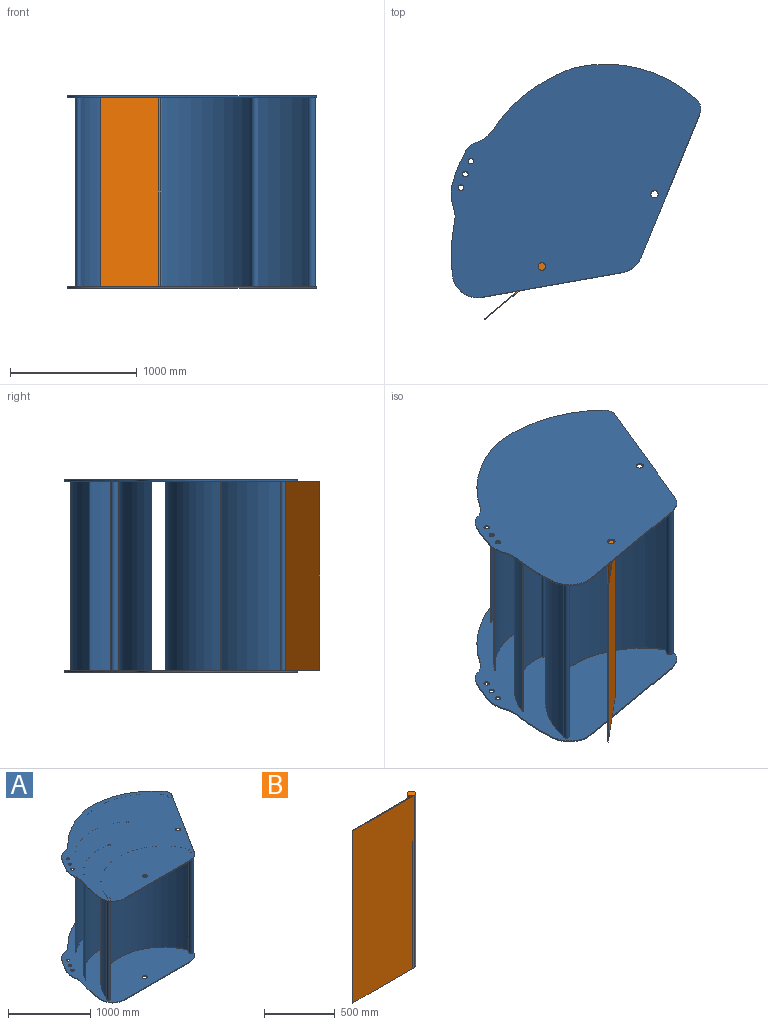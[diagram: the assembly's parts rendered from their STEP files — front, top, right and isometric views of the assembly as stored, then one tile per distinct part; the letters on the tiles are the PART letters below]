
ASSEMBLY  parts=2 mates=2
PART A: 61 faces, bbox 2164.2x1661x1520 mm
  f0: cylinder r=30.5mm len=61mm, axis (0,0,-1), area 1916.4mm2, adj f48,f49
  f1: cylinder r=29.5mm len=59mm, axis (0,0,-1), area 1853.5mm2, adj f48,f49
  f2: cylinder r=22mm len=44mm, axis (0,0,-1), area 1382.3mm2, adj f48,f49
  f3: cylinder r=22mm len=44mm, axis (0,0,-1), area 1382.3mm2, adj f48,f49
  f4: cylinder r=22mm len=44mm, axis (0,0,-1), area 1382.3mm2, adj f48,f49
  f5: cylinder r=326.18mm len=176.61mm, axis (0,0,-1), area 1797.7mm2, adj f48,f49,f50,f60
  f6: cylinder r=200mm len=212.82mm, axis (0,0,-1), area 3269.9mm2, adj f48,f49,f51,f52
  f7: cylinder r=20.5mm len=1500mm, axis (0,0,-1), area 183146.8mm2, adj f30,f44,f45,f49
  f8: cylinder r=30.5mm len=1500mm, axis (0,0,-1), area 272705.4mm2, adj f30,f44,f45,f46,f47,f49
  f9: cylinder r=15.5mm len=1500mm, axis (0,0,-1), area 135747.8mm2, adj f30,f41,f43,f49
  f10: cylinder r=15.5mm len=1500mm, axis (0,0,-1), area 136340.4mm2, adj f30,f37,f40,f49
  f11: cylinder r=30.5mm len=1500mm, axis (0,0,-1), area 274743.1mm2, adj f30,f32,f34,f35,f36,f49
  f12: cylinder r=30.5mm len=61mm, axis (0,0,-1), area 1916.4mm2, adj f30,f31
  f13: cylinder r=22mm len=44mm, axis (0,0,-1), area 1382.3mm2, adj f30,f31
  f14: cylinder r=22mm len=44mm, axis (0,0,-1), area 1382.3mm2, adj f30,f31
  f15: cylinder r=22mm len=44mm, axis (0,0,-1), area 1382.3mm2, adj f30,f31
  f16: cylinder r=29.5mm len=59mm, axis (0,0,-1), area 1853.5mm2, adj f30,f31
  f17: cylinder r=326.18mm len=176.61mm, axis (0,0,-1), area 1797.7mm2, adj f28,f29,f30,f31
  f18: cylinder r=200mm len=212.82mm, axis (0,0,-1), area 3269.9mm2, adj f19,f20,f30,f31
  f19: cylinder r=1403.06mm len=415.74mm, axis (0,0,-1), area 4273.2mm2, adj f18,f29,f30,f31
  f20: plane 1123.76x10mm, normal (0,-1,0), area 11237.6mm2, adj f18,f21,f30,f31
  f21: cylinder r=200mm len=169mm, axis (0,0,-1), area 2013.2mm2, adj f20,f22,f30,f31
  f22: plane 1036.5x655.9mm, normal (0.85,-0.53,0), area 12265.9mm2, adj f21,f23,f30,f31,f36,f47
  f23: cylinder r=100mm len=114.68mm, axis (0,0,-1), area 1222.9mm2, adj f22,f24,f30,f31
  f24: cylinder r=1074.34mm len=926.41mm, axis (0,0,-1), area 10568mm2, adj f23,f25,f30,f31
  f25: cylinder r=1282.61mm len=713.26mm, axis (0,0,-1), area 8227.7mm2, adj f24,f26,f30,f31
  f26: cylinder r=200mm len=117.51mm, axis (0,0,-1), area 1346.6mm2, adj f25,f27,f30,f31
  f27: cylinder r=186.95mm len=116.81mm, axis (0,0,-1), area 1363.1mm2, adj f26,f28,f30,f31
  f28: cylinder r=1324.47mm len=239.75mm, axis (0,0,-1), area 2828.3mm2, adj f17,f27,f30,f31
  f29: cylinder r=200mm len=107.43mm, axis (0,0,-1), area 1093.1mm2, adj f17,f19,f30,f31
  f30: plane 2164.16x1660.98mm, normal (0,0,1), area 2565292.9mm2, adj f7,f8,f9,f10,f11,f12,f13,f14
  f31: plane 2164.16x1660.98mm, normal (0,0,-1), area 2603609.2mm2, adj f12,f13,f14,f15,f16,f17,f18,f19
  f32: cylinder r=883.17mm len=1500mm, axis (0,0,-1), area 1936048.7mm2, adj f11,f30,f33,f49
  f33: plane 1500x5.5mm, normal (-0.92,-0.4,0), area 9000mm2, adj f30,f32,f34,f49
  f34: cylinder r=877.17mm len=1500mm, axis (0,0,-1), area 1914005.6mm2, adj f11,f30,f33,f49
  f35: plane 9.3x5.88mm, normal (0,0,1), area 3.7mm2, adj f11,f54
  f36: plane 9.3x5.88mm, normal (0,0,-1), area 3.7mm2, adj f11,f22
  f37: cylinder r=685.89mm len=1500mm, axis (0,0,-1), area 1444091.5mm2, adj f10,f30,f38,f49
  f38: plane 1500x4.62mm, normal (-0.77,-0.64,0), area 9000mm2, adj f30,f37,f39,f49
  f39: plane 1500x0.08mm, normal (0.65,-0.76,0), area 152.6mm2, adj f30,f38,f40,f49
  f40: cylinder r=679.89mm len=1500mm, axis (0,0,-1), area 1427930.9mm2, adj f10,f30,f39,f49
  f41: cylinder r=640.37mm len=1500mm, axis (0,0,-1), area 1242581.2mm2, adj f9,f30,f42,f49
  f42: plane 1500x5.24mm, normal (-0.49,-0.87,0), area 9000mm2, adj f30,f41,f43,f49
  f43: cylinder r=634.37mm len=1500mm, axis (0,0,-1), area 1226053.6mm2, adj f9,f30,f42,f49
  f44: cylinder r=755.25mm len=1500mm, axis (0,0,-1), area 2799788.5mm2, adj f7,f8,f30,f49
  f45: cylinder r=761.25mm len=1500mm, axis (0,0,-1), area 2838096.4mm2, adj f7,f8,f30,f49
  f46: plane 9.3x5.88mm, normal (0,0,1), area 3.7mm2, adj f8,f54
  f47: plane 9.3x5.88mm, normal (0,0,-1), area 3.7mm2, adj f8,f22
  f48: plane 2164.16x1660.98mm, normal (0,0,1), area 2603609.2mm2, adj f0,f1,f2,f3,f4,f5,f6,f50
  f49: plane 2164.16x1660.98mm, normal (0,0,-1), area 2565292.9mm2, adj f0,f1,f2,f3,f4,f5,f6,f7
  f50: cylinder r=200mm len=107.43mm, axis (0,0,-1), area 1093.1mm2, adj f5,f48,f49,f51
  f51: cylinder r=1403.06mm len=415.74mm, axis (0,0,-1), area 4273.2mm2, adj f6,f48,f49,f50
  f52: plane 1123.76x10mm, normal (0,-1,0), area 11237.6mm2, adj f6,f48,f49,f53
  f53: cylinder r=200mm len=169mm, axis (0,0,-1), area 2013.2mm2, adj f48,f49,f52,f54
  f54: plane 1036.5x655.9mm, normal (0.85,-0.53,0), area 12265.9mm2, adj f35,f46,f48,f49,f53,f55
  f55: cylinder r=100mm len=114.68mm, axis (0,0,-1), area 1222.9mm2, adj f48,f49,f54,f56
  f56: cylinder r=1074.34mm len=926.41mm, axis (0,0,-1), area 10568mm2, adj f48,f49,f55,f57
  f57: cylinder r=1282.61mm len=713.26mm, axis (0,0,-1), area 8227.7mm2, adj f48,f49,f56,f58
  f58: cylinder r=200mm len=117.51mm, axis (0,0,-1), area 1346.6mm2, adj f48,f49,f57,f59
  f59: cylinder r=186.95mm len=116.81mm, axis (0,0,-1), area 1363.1mm2, adj f48,f49,f58,f60
  f60: cylinder r=1324.47mm len=239.75mm, axis (0,0,-1), area 2828.3mm2, adj f5,f48,f49,f59
PART B: 6 faces, bbox 646.3x61x1490 mm
  f0: cylinder r=30.5mm len=1490mm, axis (0,0,-1), area 256544.7mm2, adj f1,f2,f4,f5
  f1: plane 1490x615.77mm, normal (0,-1,0), area 917501.9mm2, adj f0,f3,f4,f5
  f2: plane 1490x597.61mm, normal (0,1,0), area 890434.7mm2, adj f0,f3,f4,f5
  f3: plane 1490x6mm, normal (-1,0,0), area 8940mm2, adj f1,f2,f4,f5
  f4: plane 646.27x61mm, normal (0,0,1), area 6542.9mm2, adj f0,f1,f2,f3
  f5: plane 646.27x61mm, normal (0,0,-1), area 6542.9mm2, adj f0,f1,f2,f3
PLACE A rot(axis=(0,0,1),10deg) t=(0,0,-10)mm
PLACE B rot(axis=(0,0,1),40deg) t=(-404.65,368.46,-10)mm
MATE planar A.f0 <-> B.f0  axis (0,0,-1) through (-889.87,-570.86,750)mm
MATE revolute A.f0 <-> B.f0  axis (0,0,-1) through (-889.87,-570.86,750)mm
